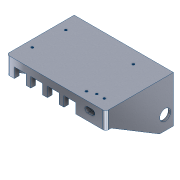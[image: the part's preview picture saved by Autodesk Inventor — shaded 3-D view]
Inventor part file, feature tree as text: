
AUTODESK INVENTOR PART (.ipt)
format: ipt  version: 2020 (Build 240168000, 168)  size: 899,584 bytes
history: native  units: in
note: dims shown in document units (in); Inventor stores cm internally (conversion verified against a paired STEP export)
features: reference x31, sketch x17, other x13, extrude x12, projected_geometry x9, plane x5, chamfer x2, helix x2, thicken_offset x1, fillet x1, mirror x1
ambient origin geometry x8: Origin, YZ Plane, XZ Plane, XY Plane, X Axis, Y Axis, Z Axis, Center Point
bodies: Solid1 (feature_tree)
feature tree (94):
  plane  "Work Plane1"
  extrude  "Extrusion1"  Depth=3.0in TaperAngle=0.0deg
  extrude  "Extrusion2"  Depth=0.25in
  sketch  "Sketch3"  dims[d11=0.005in d13=0.2in]
  plane  "Work Plane2"
  extrude  "Extrusion3"  Depth=0.005in
  thicken_offset  "Thicken1"
  extrude  "Extrusion4"  Depth=0.005in
  sketch  "Sketch5"  dims[d17=0.105in d18=0.105in]
  plane  "Work Plane3"
  extrude  "Extrusion5"  Depth=0.2in
  extrude  "Extrusion6"  Depth=0.105in
  extrude  "Extrusion7"  Depth=0.105in
  extrude  "Extrusion8"  Depth=0.089in
  extrude  "Extrusion9"  Depth=0.05in TaperAngle=45.0deg
  fillet  "Fillet1"  Radius=1.0in
  extrude  "Extrusion10"  Depth=1.0in TaperAngle=0.0deg
  mirror  "Mirror1"
  chamfer  "Chamfer1"  Distance=1.0in
  chamfer  "Chamfer2"  Distance=0.25in
  sketch  "Sketch11"  dims[d35=0.47in d36=1.0in d37=0.0in]
  plane  "Work Plane4"
  extrude  "Extrusion11"  Depth=0.325in
  helix  "Coil1"  [1 undecoded]
  sketch  "Sketch Driven Pattern1"  dims[d0=0.089in d1=3.0in d2=0.0in]
  sketch  "Sketch13"  dims[d42=0.125in d43=0.325in d44=0.1in d45=0.125in]
  plane  "Work Plane5"
  helix  "Coil2"  [1 undecoded]
  sketch  "Sketch Driven Pattern2"  dims[d5=0.0in d6=0.0in d7=0.005in]
  extrude  "Extrusion12"  Depth=0.125in
  sketch  "Sketch1"  dims[d3=0.25in d4=0.625in]
  reference  "Reference1"
  reference  "Reference2"
  reference  "Reference3"
  reference  "Reference4"
  reference  "Reference5"
  reference  "Reference6"
  reference  "Reference7"
  reference  "Reference8"
  reference  "Reference9"
  reference  "Reference10"
  reference  "Reference11"
  reference  "Reference12"
  reference  "Reference13"
  reference  "Reference14"
  sketch  "Sketch2"  dims[d8=0.3125in d9=0.0in d10=0.005in]
  reference  "Reference15"
  reference  "Reference16"
  reference  "Reference17"
  reference  "Reference18"
  sketch  "Sketch4"  dims[d14=0.1795in d15=0.0in d16=0.105in]
  reference  "Reference23"
  reference  "Reference24"
  reference  "Reference25"
  reference  "Reference26"
  reference  "Reference27"
  reference  "Reference28"
  sketch  "Sketch6"  dims[d19=0.3in d20=0.089in]
  reference  "Reference29"
  sketch  "Sketch7"  dims[d21=1.0in d22=0.0in d23=0.05in d24=0.125in d25=45.0deg]
  sketch  "Sketch8"  dims[d26=0.0125in d27=0.125in d28=45.0deg d29=1.0in d30=0.0in]
  reference  "Reference30"
  reference  "Reference31"
  sketch  "Sketch9"  dims[d31=0.0197in d32=1.0in d33=0.0in]
  reference  "Reference32"
  reference  "Reference33"
  sketch  "Sketch10"  dims[d34=0.45in]
  projected_geometry  "Projected Loop1"
  sketch  "Sketch12"  dims[d38=0.089in d40=0.25in d41=0.0in]
  projected_geometry  "Projected Loop2"
  projected_geometry  "Projected Loop3"
  projected_geometry  "Projected Loop4"
  projected_geometry  "Projected Loop5"
  projected_geometry  "Projected Loop6"
  projected_geometry  "Projected Loop7"
  projected_geometry  "Projected Loop8"
  reference  "Reference34"
  reference  "Reference35"
  sketch  "Sketch14"  dims[d46=0.125in d47=0.125in]
  projected_geometry  "Projected Loop9"
  sketch  "Sketch15"  dims[d48=0.125in d49=0.05in d50=0.0in d51=0.0in d52=0.0in d53=60.0deg d54=0.0188in d55=0.0063in d56=0.2487in d57=0.025in d58=0.2487in d59=0.3937in d60=0.0in d61=90.0deg d62=90.0deg d63=0.0in d64=0.0in d65=60.0deg d66=0.0188in d67=0.0063in d68=0.2687in d69=0.025in d70=0.2687in d71=0.3937in d72=0.0in d73=90.0deg d74=90.0deg d75=0.0in d76=0.0in d77=0.5in d78=0.375in d79=0.625in d80=1.0in d81=0.0in d82=0.25in]
  other  "<userpath>\Google Drive\Pirani Gauge\Pirani Gauge Modeling\Data Acquisition\Readout.iam"
  other  "Readout.iam"
  other  "Faceplate:1"
  other  "Gauge Controller:1"
  other  "RJ12 - 90deg:2"
  other  "RJ12 - 90deg:1"
  other  "RJ12 - 90deg:3"
  other  "RJ12 - 90deg:4"
  other  "PCB:1"
  other  "MicroUSB Breakout:1"
  other  "pcb_microusb:1"
  other  "Arduino Nano - Soldered:1"
  other  "USB-Mini-B:1"
note: 2 required parameter values undecoded (feature->parameter linkage not recoverable at this tier; creation-order binding heuristic only, values carry confidence <= 0.55)
